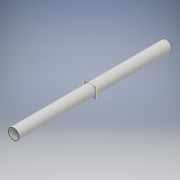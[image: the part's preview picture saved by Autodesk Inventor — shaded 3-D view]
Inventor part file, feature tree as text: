
AUTODESK INVENTOR PART (.ipt)
format: ipt  version: 2017 (Build 210142000, 142)  size: 94,208 bytes
history: native  units: mm
features: extrude x1, sketch x1
ambient origin geometry x8: Origin, YZ Plane, XZ Plane, XY Plane, X Axis, Y Axis, Z Axis, Center Point
bodies: Solid1 (feature_tree)
feature tree (2):
  extrude  "Extrusion1"  Depth=306.0mm
  sketch  "Sketch2"  dims[d0=22.0mm d1=1.0mm d2=306.0mm d3=0.0mm]
